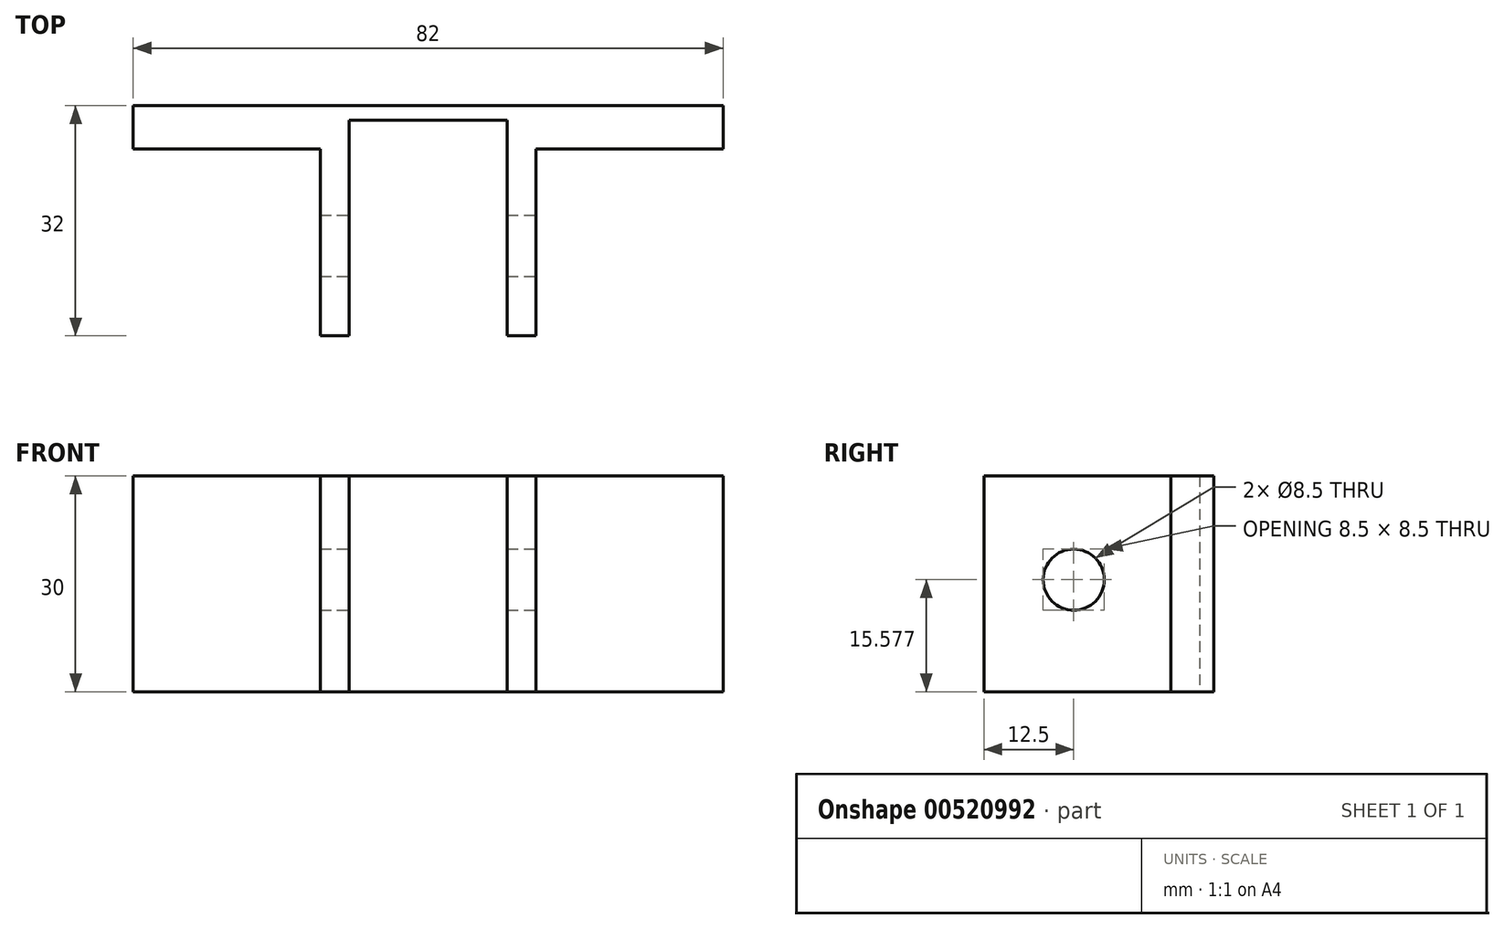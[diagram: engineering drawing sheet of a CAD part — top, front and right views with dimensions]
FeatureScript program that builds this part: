
annotation { "Feature Type Name" : "Feature", "Feature Type Description" : "" }
export const myFeature = defineFeature(function(context is Context, id is Id, definition is map)
    precondition{}
    {
        {
            var Q0;
            Q0=qCreatedBy(makeId("Top.planeOp"),FACE);
            var sketch = newSketch(context, id + "F0", { "sketchPlane" : qUnion([Q0])});
            skLineSegment(sketch, "E0", {"start": v(11, 0) * mm, "end": v(11, 30) * mm});
            skLineSegment(sketch, "E1", {"start": v(11, 30) * mm, "end": v(41, 30) * mm});
            skLineSegment(sketch, "E2", {"start": v(41, 30) * mm, "end": v(41, 26) * mm});
            skLineSegment(sketch, "E3", {"start": v(41, 26) * mm, "end": v(15, 26) * mm});
            skLineSegment(sketch, "E4", {"start": v(15, 26) * mm, "end": v(15, 0) * mm});
            skLineSegment(sketch, "E5", {"start": v(15, 0) * mm, "end": v(11, 0) * mm});
            skLineSegment(sketch, "E6", {"start": v(0, -1.27) * mm, "end": v(0, 36.68) * mm, "construction": true});
            skLineSegment(sketch, "E7.MirrorCS", {"start": v(-41, 30) * mm, "end": v(-41, 26) * mm});
            skLineSegment(sketch, "E8.MirrorCS", {"start": v(-15, 0) * mm, "end": v(-11, 0) * mm});
            skLineSegment(sketch, "E9.MirrorCS", {"start": v(-11, 0) * mm, "end": v(-11, 30) * mm});
            skLineSegment(sketch, "E10.MirrorCS", {"start": v(-11, 30) * mm, "end": v(-41, 30) * mm});
            skLineSegment(sketch, "E11.MirrorCS", {"start": v(-41, 26) * mm, "end": v(-15, 26) * mm});
            skLineSegment(sketch, "E12.MirrorCS", {"start": v(-15, 26) * mm, "end": v(-15, 0) * mm});
            skLineSegment(sketch, "E13", {"start": v(-41, 30) * mm, "end": v(41, 30) * mm});
            skLineSegment(sketch, "E14", {"start": v(41, 30) * mm, "end": v(41, 32) * mm});
            skLineSegment(sketch, "E15", {"start": v(41, 32) * mm, "end": v(-41, 32) * mm});
            skLineSegment(sketch, "E16", {"start": v(-41, 32) * mm, "end": v(-41, 30) * mm});
            skSolve(sketch);
        }
        {
            var Q0;
            Q0 = qSketchRegion(id + "F0", true);
            extrude(context, id + "F1", {"entities" : qUnion([Q0]), "depth" : 30 * mm, "offsetDistance" : 25 * mm});
        }
        {
            var Q0;
            Q0=qCreatedBy(makeId("Right.planeOp"),FACE);
            var sketch = newSketch(context, id + "F2", { "sketchPlane" : qUnion([Q0])});
            skCircle(sketch, "E17", {"center": v(12.5, 15.58) * mm, "radius": 4.25 * mm});
            skLineSegment(sketch, "E18", {"start": v(26, 0) * mm, "end": v(0, 30) * mm, "construction": true});
            skSolve(sketch);
        }
        {
            var Q0;
            Q0 = qSketchRegion(id + "F2", true);
            extrude(context, id + "F3", {"entities" : qUnion([Q0]), "operationType" : NewBodyOperationType.REMOVE, "endBound" : BoundingType.THROUGH_ALL, "oppositeDirection" : true, "depth" : 25 * mm, "offsetDistance" : 25 * mm, "hasSecondDirection" : true, "secondDirectionBound" : SecondDirectionBoundingType.THROUGH_ALL, "secondDirectionOppositeDirection" : false, "secondDirectionDepth" : 25 * mm});
        }
    });
